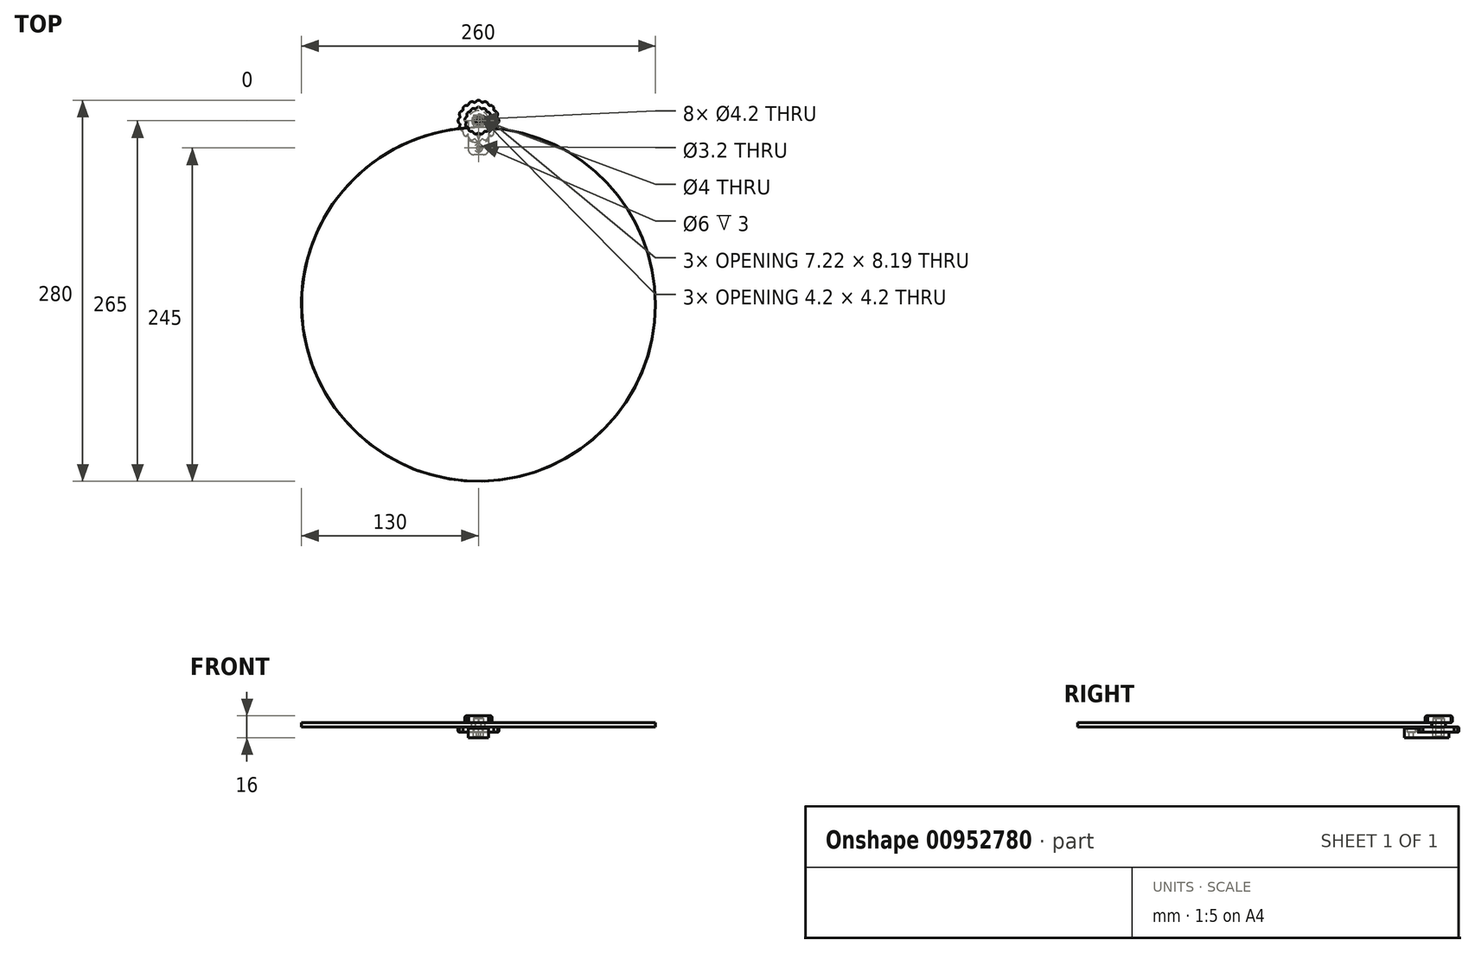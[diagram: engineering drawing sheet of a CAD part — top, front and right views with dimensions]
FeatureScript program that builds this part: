
annotation { "Feature Type Name" : "Feature", "Feature Type Description" : "" }
export const myFeature = defineFeature(function(context is Context, id is Id, definition is map)
    precondition{}
    {
        {
            var Q0;
            Q0=qCreatedBy(makeId("Top.planeOp"),FACE);
            var sketch = newSketch(context, id + "F0", { "sketchPlane" : qUnion([Q0])});
            skCircle(sketch, "E0", {"center": v(0, 0) * mm, "radius": 130 * mm});
            skSolve(sketch);
        }
        {
            var Q0;
            Q0=qCreatedBy(makeId("Top.planeOp"),FACE);
            var sketch = newSketch(context, id + "F1", { "sketchPlane" : qUnion([Q0])});
            skArc(sketch, "E1.0", {"start": v(7.5, 119.77) * mm, "mid": v(0, 120) * mm, "end": v(-7.5, 119.77) * mm});
            skLineSegment(sketch, "E2", {"start": v(0, 146.3) * mm, "end": v(0, 110.4) * mm});
            skLineSegment(sketch, "E3.0", {"start": v(-7.5, 146.3) * mm, "end": v(-7.5, 110.4) * mm});
            skLineSegment(sketch, "E4.0", {"start": v(7.5, 146.3) * mm, "end": v(7.5, 110.4) * mm});
            skArc(sketch, "E5.0", {"start": v(7.5, 129.78) * mm, "mid": v(0, 130) * mm, "end": v(-7.5, 129.78) * mm});
            skArc(sketch, "E6", {"start": v(7.5, 132.5) * mm, "mid": v(0, 140) * mm, "end": v(-7.5, 132.5) * mm});
            skSolve(sketch);
        }
        {
            var Q0;
            Q0 = qSketchRegion(id + "F1", true);
            extrude(context, id + "F2", {"entities" : qUnion([Q0]), "depth" : 4 * mm, "offsetDistance" : 25 * mm});
        }
        {
            var Q0;
            Q0=makeQuery(id+"F2.opExtrude","CAP_FACE",FACE,{"disambiguationData":[OSD([sQuery(id+"F1.wireOp",EDGE,"E1.0"),sQuery(id+"F1.wireOp",EDGE,"E3.0"),sQuery(id+"F1.wireOp",EDGE,"E4.0"),sQuery(id+"F1.wireOp",EDGE,"E6")])],"isStart":false});
            var sketch = newSketch(context, id + "F3", { "sketchPlane" : qUnion([Q0])});
            skArc(sketch, "E7.0", {"start": v(7.5, 129.78) * mm, "mid": v(0, 130) * mm, "end": v(-7.5, 129.78) * mm});
            skLineSegment(sketch, "E8.0", {"start": v(-7.5, 132.5) * mm, "end": v(-7.5, 119.77) * mm});
            skPoint(sketch, "E9.0", {"position": v(7.5, 132.5) * mm});
            skLineSegment(sketch, "E10.0", {"start": v(7.5, 132.5) * mm, "end": v(7.5, 119.77) * mm});
            skArc(sketch, "E11.0", {"start": v(7.5, 119.77) * mm, "mid": v(0, 120) * mm, "end": v(-7.5, 119.77) * mm});
            skSolve(sketch);
        }
        {
            var Q0;
            Q0 = qSketchRegion(id + "F3", true);
            extrude(context, id + "F4", {"entities" : qUnion([Q0]), "operationType" : NewBodyOperationType.REMOVE, "oppositeDirection" : true, "depth" : 3 * mm, "offsetDistance" : 25 * mm});
        }
        {
            var Q0;
            Q0=makeQuery(id+"F2.opExtrude","SWEPT_EDGE",EDGE,{"disambiguationData":[OSD([sQuery(id+"F1.wireOp",EDGE,"E1.0"),sQuery(id+"F1.wireOp",EDGE,"E4.0")])]});
            var Q1;
            Q1=makeQuery(id+"F2.opExtrude","SWEPT_EDGE",EDGE,{"disambiguationData":[OSD([sQuery(id+"F1.wireOp",EDGE,"E1.0"),sQuery(id+"F1.wireOp",EDGE,"E3.0")])]});
            fillet(context, id + "F5", {"entities" : qUnion([Q0, Q1]), "radius" : 5 * mm, "tangentPropagation" : true, "allowEdgeOverflow" : false});
        }
        {
            var Q0;
            Q0=makeQuery(id+"F2.opExtrude","CAP_FACE",FACE,{"disambiguationData":[OSD([sQuery(id+"F1.wireOp",EDGE,"E1.0"),sQuery(id+"F1.wireOp",EDGE,"E3.0"),sQuery(id+"F1.wireOp",EDGE,"E4.0"),sQuery(id+"F1.wireOp",EDGE,"E6")])],"isStart":false});
            var sketch = newSketch(context, id + "F6", { "sketchPlane" : qUnion([Q0])});
            skLineSegment(sketch, "E12", {"start": v(0, 140) * mm, "end": v(0, 130) * mm, "construction": true});
            skCircle(sketch, "E13", {"center": v(0, 135) * mm, "radius": 1.6 * mm});
            skSolve(sketch);
        }
        {
            var Q0;
            Q0=makeQuery(id+"F6.imprint","IMPRINT",FACE,{"disambiguationData":[TD([[makeQuery(id+"F6.imprint","IMPRINT",EDGE,{"derivedFrom":sQuery(id+"F6.wireOp",EDGE,"E13")}),1.0]])]});
            extrude(context, id + "F7", {"entities" : qUnion([Q0]), "operationType" : NewBodyOperationType.REMOVE, "oppositeDirection" : true, "depth" : 25 * mm, "offsetDistance" : 25 * mm});
        }
        {
            var Q0;
            Q0=makeQuery(id+"F2.opExtrude","CAP_FACE",FACE,{"disambiguationData":[OSD([sQuery(id+"F1.wireOp",EDGE,"E1.0"),sQuery(id+"F1.wireOp",EDGE,"E3.0"),sQuery(id+"F1.wireOp",EDGE,"E4.0"),sQuery(id+"F1.wireOp",EDGE,"E6")])],"isStart":true});
            var sketch = newSketch(context, id + "F8", { "sketchPlane" : qUnion([Q0])});
            skPoint(sketch, "E14.center", {"position": v(0, -135) * mm});
            skArc(sketch, "E15", {"start": v(-1.6, -144.19) * mm, "mid": v(0, -145) * mm, "end": v(1.6, -144.19) * mm});
            skArc(sketch, "E16.1.0", {"start": v(2.85, -143.88) * mm, "mid": v(4.65, -143.85) * mm, "end": v(5.7, -142.39) * mm});
            skArc(sketch, "E16.2.0", {"start": v(6.65, -141.54) * mm, "mid": v(8.23, -140.68) * mm, "end": v(8.48, -138.9) * mm});
            skArc(sketch, "E16.3.0", {"start": v(8.93, -137.7) * mm, "mid": v(9.93, -136.2) * mm, "end": v(9.32, -134.51) * mm});
            skArc(sketch, "E16.4.0", {"start": v(9.16, -133.24) * mm, "mid": v(9.35, -131.45) * mm, "end": v(8.02, -130.24) * mm});
            skArc(sketch, "E16.5.0", {"start": v(7.3, -129.19) * mm, "mid": v(6.63, -127.51) * mm, "end": v(4.9, -127.06) * mm});
            skArc(sketch, "E16.6.0", {"start": v(3.76, -126.46) * mm, "mid": v(2.4, -125.3) * mm, "end": v(0.64, -125.7) * mm});
            skArc(sketch, "E16.7.0", {"start": v(-0.64, -125.7) * mm, "mid": v(-2.4, -125.3) * mm, "end": v(-3.76, -126.46) * mm});
            skArc(sketch, "E16.8.0", {"start": v(-4.9, -127.06) * mm, "mid": v(-6.63, -127.51) * mm, "end": v(-7.3, -129.19) * mm});
            skArc(sketch, "E16.9.0", {"start": v(-8.02, -130.24) * mm, "mid": v(-9.35, -131.45) * mm, "end": v(-9.16, -133.24) * mm});
            skArc(sketch, "E16.10.0", {"start": v(-9.32, -134.51) * mm, "mid": v(-9.93, -136.2) * mm, "end": v(-8.93, -137.7) * mm});
            skArc(sketch, "E16.11.0", {"start": v(-8.48, -138.9) * mm, "mid": v(-8.23, -140.68) * mm, "end": v(-6.65, -141.54) * mm});
            skArc(sketch, "E16.12.0", {"start": v(-5.7, -142.39) * mm, "mid": v(-4.65, -143.85) * mm, "end": v(-2.85, -143.88) * mm});
            skPoint(sketch, "E17.newPointA", {"position": v(-5.25, -141.04) * mm});
            skPoint(sketch, "E17.newPointB", {"position": v(-5.36, -140.94) * mm});
            skArc(sketch, "E17.filletArc", {"start": v(-5.7, -142.39) * mm, "mid": v(-6.02, -141.8) * mm, "end": v(-6.65, -141.54) * mm});
            skPoint(sketch, "E18.newPointA", {"position": v(-1.84, -142.78) * mm});
            skPoint(sketch, "E18.newPointB", {"position": v(-1.98, -142.75) * mm});
            skArc(sketch, "E18.filletArc", {"start": v(-1.6, -144.19) * mm, "mid": v(-2.17, -143.81) * mm, "end": v(-2.85, -143.88) * mm});
            skPoint(sketch, "E19.newPointA", {"position": v(1.98, -142.75) * mm});
            skPoint(sketch, "E19.newPointB", {"position": v(1.84, -142.78) * mm});
            skArc(sketch, "E19.filletArc", {"start": v(2.85, -143.88) * mm, "mid": v(2.17, -143.81) * mm, "end": v(1.6, -144.19) * mm});
            skPoint(sketch, "E20.newPointA", {"position": v(5.36, -140.94) * mm});
            skPoint(sketch, "E20.newPointB", {"position": v(5.25, -141.04) * mm});
            skArc(sketch, "E20.filletArc", {"start": v(6.65, -141.54) * mm, "mid": v(6.02, -141.8) * mm, "end": v(5.7, -142.39) * mm});
            skPoint(sketch, "E21.newPointA", {"position": v(7.5, -137.77) * mm});
            skPoint(sketch, "E21.newPointB", {"position": v(7.45, -137.9) * mm});
            skArc(sketch, "E21.filletArc", {"start": v(8.93, -137.7) * mm, "mid": v(8.49, -138.22) * mm, "end": v(8.48, -138.9) * mm});
            skPoint(sketch, "E22.newPointA", {"position": v(7.93, -133.96) * mm});
            skPoint(sketch, "E22.newPointB", {"position": v(7.95, -134.1) * mm});
            skArc(sketch, "E22.filletArc", {"start": v(9.16, -133.24) * mm, "mid": v(9.01, -133.9) * mm, "end": v(9.32, -134.51) * mm});
            skPoint(sketch, "E23.newPointA", {"position": v(6.54, -130.4) * mm});
            skPoint(sketch, "E23.newPointB", {"position": v(6.62, -130.51) * mm});
            skArc(sketch, "E23.filletArc", {"start": v(7.3, -129.19) * mm, "mid": v(7.47, -129.84) * mm, "end": v(8.02, -130.24) * mm});
            skPoint(sketch, "E24.newPointA", {"position": v(3.65, -127.88) * mm});
            skPoint(sketch, "E24.newPointB", {"position": v(3.78, -127.95) * mm});
            skArc(sketch, "E24.filletArc", {"start": v(3.76, -126.46) * mm, "mid": v(4.22, -126.96) * mm, "end": v(4.9, -127.06) * mm});
            skPoint(sketch, "E25.newPointA", {"position": v(-0.07, -127) * mm});
            skPoint(sketch, "E25.newPointB", {"position": v(0.07, -127) * mm});
            skArc(sketch, "E25.filletArc", {"start": v(-0.64, -125.7) * mm, "mid": v(0, -125.92) * mm, "end": v(0.64, -125.7) * mm});
            skPoint(sketch, "E26.newPointA", {"position": v(-3.78, -127.95) * mm});
            skPoint(sketch, "E26.newPointB", {"position": v(-3.65, -127.88) * mm});
            skArc(sketch, "E26.filletArc", {"start": v(-4.9, -127.06) * mm, "mid": v(-4.22, -126.96) * mm, "end": v(-3.76, -126.46) * mm});
            skPoint(sketch, "E27.newPointA", {"position": v(-6.54, -130.4) * mm});
            skPoint(sketch, "E27.newPointB", {"position": v(-6.62, -130.51) * mm});
            skArc(sketch, "E27.filletArc", {"start": v(-8.02, -130.24) * mm, "mid": v(-7.47, -129.84) * mm, "end": v(-7.3, -129.19) * mm});
            skPoint(sketch, "E28.newPointA", {"position": v(-7.95, -134.1) * mm});
            skPoint(sketch, "E28.newPointB", {"position": v(-7.93, -133.96) * mm});
            skArc(sketch, "E28.filletArc", {"start": v(-9.32, -134.51) * mm, "mid": v(-9.01, -133.9) * mm, "end": v(-9.16, -133.24) * mm});
            skPoint(sketch, "E29.newPointA", {"position": v(-7.45, -137.9) * mm});
            skPoint(sketch, "E29.newPointB", {"position": v(-7.5, -137.77) * mm});
            skArc(sketch, "E29.filletArc", {"start": v(-8.48, -138.9) * mm, "mid": v(-8.49, -138.22) * mm, "end": v(-8.93, -137.7) * mm});
            skSolve(sketch);
        }
        {
            var Q0;
            Q0 = qSketchRegion(id + "F8", true);
            extrude(context, id + "F9", {"entities" : qUnion([Q0]), "depth" : 5 * mm, "offsetDistance" : 25 * mm});
        }
        {
            var Q0;
            Q0=makeQuery(id+"F9.opExtrude","CAP_FACE",FACE,{"disambiguationData":[OSD([sQuery(id+"F8.wireOp",EDGE,"E15"),sQuery(id+"F8.wireOp",EDGE,"E16.1.0"),sQuery(id+"F8.wireOp",EDGE,"E16.2.0"),sQuery(id+"F8.wireOp",EDGE,"E16.3.0"),sQuery(id+"F8.wireOp",EDGE,"E16.4.0"),sQuery(id+"F8.wireOp",EDGE,"E16.5.0"),sQuery(id+"F8.wireOp",EDGE,"E16.6.0"),sQuery(id+"F8.wireOp",EDGE,"E16.7.0"),sQuery(id+"F8.wireOp",EDGE,"E16.8.0"),sQuery(id+"F8.wireOp",EDGE,"E16.9.0"),sQuery(id+"F8.wireOp",EDGE,"E16.10.0"),sQuery(id+"F8.wireOp",EDGE,"E16.11.0"),sQuery(id+"F8.wireOp",EDGE,"E16.12.0"),sQuery(id+"F8.wireOp",EDGE,"E17.filletArc"),sQuery(id+"F8.wireOp",EDGE,"E18.filletArc"),sQuery(id+"F8.wireOp",EDGE,"E19.filletArc"),sQuery(id+"F8.wireOp",EDGE,"E20.filletArc"),sQuery(id+"F8.wireOp",EDGE,"E21.filletArc"),sQuery(id+"F8.wireOp",EDGE,"E22.filletArc"),sQuery(id+"F8.wireOp",EDGE,"E23.filletArc"),sQuery(id+"F8.wireOp",EDGE,"E24.filletArc"),sQuery(id+"F8.wireOp",EDGE,"E25.filletArc"),sQuery(id+"F8.wireOp",EDGE,"E26.filletArc"),sQuery(id+"F8.wireOp",EDGE,"E27.filletArc"),sQuery(id+"F8.wireOp",EDGE,"E28.filletArc"),sQuery(id+"F8.wireOp",EDGE,"E29.filletArc")])],"isStart":true});
            var Q1;
            Q1=makeQuery(id+"F9.opExtrude","CAP_FACE",FACE,{"disambiguationData":[OSD([sQuery(id+"F8.wireOp",EDGE,"E15"),sQuery(id+"F8.wireOp",EDGE,"E16.1.0"),sQuery(id+"F8.wireOp",EDGE,"E16.2.0"),sQuery(id+"F8.wireOp",EDGE,"E16.3.0"),sQuery(id+"F8.wireOp",EDGE,"E16.4.0"),sQuery(id+"F8.wireOp",EDGE,"E16.5.0"),sQuery(id+"F8.wireOp",EDGE,"E16.6.0"),sQuery(id+"F8.wireOp",EDGE,"E16.7.0"),sQuery(id+"F8.wireOp",EDGE,"E16.8.0"),sQuery(id+"F8.wireOp",EDGE,"E16.9.0"),sQuery(id+"F8.wireOp",EDGE,"E16.10.0"),sQuery(id+"F8.wireOp",EDGE,"E16.11.0"),sQuery(id+"F8.wireOp",EDGE,"E16.12.0"),sQuery(id+"F8.wireOp",EDGE,"E17.filletArc"),sQuery(id+"F8.wireOp",EDGE,"E18.filletArc"),sQuery(id+"F8.wireOp",EDGE,"E19.filletArc"),sQuery(id+"F8.wireOp",EDGE,"E20.filletArc"),sQuery(id+"F8.wireOp",EDGE,"E21.filletArc"),sQuery(id+"F8.wireOp",EDGE,"E22.filletArc"),sQuery(id+"F8.wireOp",EDGE,"E23.filletArc"),sQuery(id+"F8.wireOp",EDGE,"E24.filletArc"),sQuery(id+"F8.wireOp",EDGE,"E25.filletArc"),sQuery(id+"F8.wireOp",EDGE,"E26.filletArc"),sQuery(id+"F8.wireOp",EDGE,"E27.filletArc"),sQuery(id+"F8.wireOp",EDGE,"E28.filletArc"),sQuery(id+"F8.wireOp",EDGE,"E29.filletArc")])],"isStart":false});
            fillet(context, id + "F10", {"entities" : qUnion([Q0, Q1]), "radius" : 1 * mm, "tangentPropagation" : true, "allowEdgeOverflow" : false});
        }
        {
            var Q0;
            Q0=makeQuery(id+"F9.opExtrude","CAP_FACE",FACE,{"disambiguationData":[OSD([sQuery(id+"F8.wireOp",EDGE,"E15"),sQuery(id+"F8.wireOp",EDGE,"E16.1.0"),sQuery(id+"F8.wireOp",EDGE,"E16.2.0"),sQuery(id+"F8.wireOp",EDGE,"E16.3.0"),sQuery(id+"F8.wireOp",EDGE,"E16.4.0"),sQuery(id+"F8.wireOp",EDGE,"E16.5.0"),sQuery(id+"F8.wireOp",EDGE,"E16.6.0"),sQuery(id+"F8.wireOp",EDGE,"E16.7.0"),sQuery(id+"F8.wireOp",EDGE,"E16.8.0"),sQuery(id+"F8.wireOp",EDGE,"E16.9.0"),sQuery(id+"F8.wireOp",EDGE,"E16.10.0"),sQuery(id+"F8.wireOp",EDGE,"E16.11.0"),sQuery(id+"F8.wireOp",EDGE,"E16.12.0"),sQuery(id+"F8.wireOp",EDGE,"E17.filletArc"),sQuery(id+"F8.wireOp",EDGE,"E18.filletArc"),sQuery(id+"F8.wireOp",EDGE,"E19.filletArc"),sQuery(id+"F8.wireOp",EDGE,"E20.filletArc"),sQuery(id+"F8.wireOp",EDGE,"E21.filletArc"),sQuery(id+"F8.wireOp",EDGE,"E22.filletArc"),sQuery(id+"F8.wireOp",EDGE,"E23.filletArc"),sQuery(id+"F8.wireOp",EDGE,"E24.filletArc"),sQuery(id+"F8.wireOp",EDGE,"E25.filletArc"),sQuery(id+"F8.wireOp",EDGE,"E26.filletArc"),sQuery(id+"F8.wireOp",EDGE,"E27.filletArc"),sQuery(id+"F8.wireOp",EDGE,"E28.filletArc"),sQuery(id+"F8.wireOp",EDGE,"E29.filletArc")])],"isStart":false});
            var sketch = newSketch(context, id + "F11", { "sketchPlane" : qUnion([Q0])});
            skCircle(sketch, "E30", {"center": v(0, -135) * mm, "radius": 4.9 * mm});
            skSolve(sketch);
        }
        {
            var Q0;
            Q0 = qSketchRegion(id + "F11", true);
            extrude(context, id + "F12", {"entities" : qUnion([Q0]), "depth" : 3 * mm, "offsetDistance" : 25 * mm});
        }
        {
            var Q0;
            Q0=makeQuery(id+"F12.opExtrude","CAP_FACE",FACE,{"disambiguationData":[OSD([sQuery(id+"F11.wireOp",EDGE,"E30")])],"isStart":false});
            var sketch = newSketch(context, id + "F13", { "sketchPlane" : qUnion([Q0])});
            skLineSegment(sketch, "E31", {"start": v(0, -135) * mm, "end": v(17.48, -135) * mm, "construction": true});
            skArc(sketch, "E32", {"start": v(12.25, -137.49) * mm, "mid": v(15, -135) * mm, "end": v(12.25, -132.51) * mm});
            skArc(sketch, "E33.1.0", {"start": v(12.27, -132.61) * mm, "mid": v(13.86, -129.26) * mm, "end": v(10.37, -128.01) * mm});
            skArc(sketch, "E33.2.0", {"start": v(10.42, -128.1) * mm, "mid": v(10.6, -124.4) * mm, "end": v(6.9, -124.58) * mm});
            skArc(sketch, "E33.3.0", {"start": v(6.99, -124.63) * mm, "mid": v(5.74, -121.14) * mm, "end": v(2.39, -122.73) * mm});
            skArc(sketch, "E33.4.0", {"start": v(2.49, -122.75) * mm, "mid": v(0, -120) * mm, "end": v(-2.49, -122.75) * mm});
            skArc(sketch, "E33.5.0", {"start": v(-2.39, -122.73) * mm, "mid": v(-5.74, -121.14) * mm, "end": v(-6.99, -124.63) * mm});
            skArc(sketch, "E33.6.0", {"start": v(-6.9, -124.58) * mm, "mid": v(-10.6, -124.4) * mm, "end": v(-10.42, -128.1) * mm});
            skArc(sketch, "E33.7.0", {"start": v(-10.37, -128.01) * mm, "mid": v(-13.86, -129.26) * mm, "end": v(-12.27, -132.61) * mm});
            skArc(sketch, "E33.8.0", {"start": v(-12.25, -132.51) * mm, "mid": v(-15, -135) * mm, "end": v(-12.25, -137.49) * mm});
            skArc(sketch, "E33.9.0", {"start": v(-12.27, -137.39) * mm, "mid": v(-13.86, -140.74) * mm, "end": v(-10.37, -141.99) * mm});
            skArc(sketch, "E33.10.0", {"start": v(-10.42, -141.9) * mm, "mid": v(-10.6, -145.6) * mm, "end": v(-6.9, -145.42) * mm});
            skArc(sketch, "E33.11.0", {"start": v(-6.99, -145.37) * mm, "mid": v(-5.74, -148.86) * mm, "end": v(-2.39, -147.27) * mm});
            skArc(sketch, "E33.12.0", {"start": v(-2.49, -147.25) * mm, "mid": v(0, -150) * mm, "end": v(2.49, -147.25) * mm});
            skArc(sketch, "E33.13.0", {"start": v(2.39, -147.27) * mm, "mid": v(5.74, -148.86) * mm, "end": v(6.99, -145.37) * mm});
            skArc(sketch, "E33.14.0", {"start": v(6.9, -145.42) * mm, "mid": v(10.6, -145.6) * mm, "end": v(10.42, -141.9) * mm});
            skArc(sketch, "E33.15.0", {"start": v(10.37, -141.99) * mm, "mid": v(13.86, -140.74) * mm, "end": v(12.27, -137.39) * mm});
            skPoint(sketch, "E33.center", {"position": v(0, -135) * mm});
            skSolve(sketch);
        }
        {
            var Q0;
            Q0 = qSketchRegion(id + "F13", true);
            extrude(context, id + "F14", {"entities" : qUnion([Q0]), "operationType" : NewBodyOperationType.ADD, "depth" : 4 * mm, "offsetDistance" : 25 * mm});
        }
        {
            var Q0;
            Q0=makeQuery(id+"F14.opExtrude","SWEPT_EDGE",EDGE,{"disambiguationData":[OSD([sQuery(id+"F13.wireOp",EDGE,"E33.1.0"),sQuery(id+"F13.wireOp",EDGE,"E33.2.0")])]});
            var Q1;
            Q1=makeQuery(id+"F14.opExtrude","SWEPT_EDGE",EDGE,{"disambiguationData":[OSD([sQuery(id+"F13.wireOp",EDGE,"E32"),sQuery(id+"F13.wireOp",EDGE,"E33.1.0")])]});
            var Q2;
            Q2=makeQuery(id+"F14.opExtrude","SWEPT_EDGE",EDGE,{"disambiguationData":[OSD([sQuery(id+"F13.wireOp",EDGE,"E33.2.0"),sQuery(id+"F13.wireOp",EDGE,"E33.3.0")])]});
            var Q3;
            Q3=makeQuery(id+"F14.opExtrude","SWEPT_EDGE",EDGE,{"disambiguationData":[OSD([sQuery(id+"F13.wireOp",EDGE,"E33.3.0"),sQuery(id+"F13.wireOp",EDGE,"E33.4.0")])]});
            var Q4;
            Q4=makeQuery(id+"F14.opExtrude","SWEPT_EDGE",EDGE,{"disambiguationData":[OSD([sQuery(id+"F13.wireOp",EDGE,"E33.4.0"),sQuery(id+"F13.wireOp",EDGE,"E33.5.0")])]});
            var Q5;
            Q5=makeQuery(id+"F14.opExtrude","SWEPT_EDGE",EDGE,{"disambiguationData":[OSD([sQuery(id+"F13.wireOp",EDGE,"E33.5.0"),sQuery(id+"F13.wireOp",EDGE,"E33.6.0")])]});
            var Q6;
            Q6=makeQuery(id+"F14.opExtrude","SWEPT_EDGE",EDGE,{"disambiguationData":[OSD([sQuery(id+"F13.wireOp",EDGE,"E33.6.0"),sQuery(id+"F13.wireOp",EDGE,"E33.7.0")])]});
            var Q7;
            Q7=makeQuery(id+"F14.opExtrude","SWEPT_EDGE",EDGE,{"disambiguationData":[OSD([sQuery(id+"F13.wireOp",EDGE,"E33.7.0"),sQuery(id+"F13.wireOp",EDGE,"E33.8.0")])]});
            var Q8;
            Q8=makeQuery(id+"F14.opExtrude","SWEPT_EDGE",EDGE,{"disambiguationData":[OSD([sQuery(id+"F13.wireOp",EDGE,"E33.8.0"),sQuery(id+"F13.wireOp",EDGE,"E33.9.0")])]});
            var Q9;
            Q9=makeQuery(id+"F14.opExtrude","SWEPT_EDGE",EDGE,{"disambiguationData":[OSD([sQuery(id+"F13.wireOp",EDGE,"E33.9.0"),sQuery(id+"F13.wireOp",EDGE,"E33.10.0")])]});
            var Q10;
            Q10=makeQuery(id+"F14.opExtrude","SWEPT_EDGE",EDGE,{"disambiguationData":[OSD([sQuery(id+"F13.wireOp",EDGE,"E33.10.0"),sQuery(id+"F13.wireOp",EDGE,"E33.11.0")])]});
            var Q11;
            Q11=makeQuery(id+"F14.opExtrude","SWEPT_EDGE",EDGE,{"disambiguationData":[OSD([sQuery(id+"F13.wireOp",EDGE,"E33.11.0"),sQuery(id+"F13.wireOp",EDGE,"E33.12.0")])]});
            var Q12;
            Q12=makeQuery(id+"F14.opExtrude","SWEPT_EDGE",EDGE,{"disambiguationData":[OSD([sQuery(id+"F13.wireOp",EDGE,"E33.12.0"),sQuery(id+"F13.wireOp",EDGE,"E33.13.0")])]});
            var Q13;
            Q13=makeQuery(id+"F14.opExtrude","SWEPT_EDGE",EDGE,{"disambiguationData":[OSD([sQuery(id+"F13.wireOp",EDGE,"E33.13.0"),sQuery(id+"F13.wireOp",EDGE,"E33.14.0")])]});
            var Q14;
            Q14=makeQuery(id+"F14.opExtrude","SWEPT_EDGE",EDGE,{"disambiguationData":[OSD([sQuery(id+"F13.wireOp",EDGE,"E33.14.0"),sQuery(id+"F13.wireOp",EDGE,"E33.15.0")])]});
            var Q15;
            Q15=makeQuery(id+"F14.opExtrude","SWEPT_EDGE",EDGE,{"disambiguationData":[OSD([sQuery(id+"F13.wireOp",EDGE,"E32"),sQuery(id+"F13.wireOp",EDGE,"E33.15.0")])]});
            fillet(context, id + "F15", {"entities" : qUnion([Q0, Q1, Q2, Q3, Q4, Q5, Q6, Q7, Q8, Q9, Q10, Q11, Q12, Q13, Q14, Q15]), "radius" : 1 * mm, "tangentPropagation" : true, "allowEdgeOverflow" : false});
        }
        {
            var Q0;
            Q0=makeQuery(id+"F14.opExtrude","CAP_EDGE",EDGE,{"disambiguationData":[OSD([sQuery(id+"F13.wireOp",EDGE,"E33.13.0")])],"isStart":true});
            var Q1;
            Q1=makeQuery(id+"F14.opExtrude","CAP_EDGE",EDGE,{"disambiguationData":[OSD([sQuery(id+"F13.wireOp",EDGE,"E33.14.0")])],"isStart":false});
            fillet(context, id + "F16", {"entities" : qUnion([Q0, Q1]), "radius" : 1 * mm, "tangentPropagation" : true, "allowEdgeOverflow" : false});
        }
        {
            var Q0;
            Q0=makeQuery(id+"F2.opExtrude","SWEPT_BODY",BODY,{"disambiguationData":[OSD([sQuery(id+"F1.wireOp",EDGE,"E1.0"),sQuery(id+"F1.wireOp",EDGE,"E3.0"),sQuery(id+"F1.wireOp",EDGE,"E4.0"),sQuery(id+"F1.wireOp",EDGE,"E6")])]});
            deleteBodies(context, id + "F17", {"entities" : qUnion([Q0])});
        }
        {
            var Q0;
            Q0=makeQuery(id+"F9.opExtrude","CAP_FACE",FACE,{"disambiguationData":[OSD([sQuery(id+"F8.wireOp",EDGE,"E15"),sQuery(id+"F8.wireOp",EDGE,"E16.1.0"),sQuery(id+"F8.wireOp",EDGE,"E16.2.0"),sQuery(id+"F8.wireOp",EDGE,"E16.3.0"),sQuery(id+"F8.wireOp",EDGE,"E16.4.0"),sQuery(id+"F8.wireOp",EDGE,"E16.5.0"),sQuery(id+"F8.wireOp",EDGE,"E16.6.0"),sQuery(id+"F8.wireOp",EDGE,"E16.7.0"),sQuery(id+"F8.wireOp",EDGE,"E16.8.0"),sQuery(id+"F8.wireOp",EDGE,"E16.9.0"),sQuery(id+"F8.wireOp",EDGE,"E16.10.0"),sQuery(id+"F8.wireOp",EDGE,"E16.11.0"),sQuery(id+"F8.wireOp",EDGE,"E16.12.0"),sQuery(id+"F8.wireOp",EDGE,"E17.filletArc"),sQuery(id+"F8.wireOp",EDGE,"E18.filletArc"),sQuery(id+"F8.wireOp",EDGE,"E19.filletArc"),sQuery(id+"F8.wireOp",EDGE,"E20.filletArc"),sQuery(id+"F8.wireOp",EDGE,"E21.filletArc"),sQuery(id+"F8.wireOp",EDGE,"E22.filletArc"),sQuery(id+"F8.wireOp",EDGE,"E23.filletArc"),sQuery(id+"F8.wireOp",EDGE,"E24.filletArc"),sQuery(id+"F8.wireOp",EDGE,"E25.filletArc"),sQuery(id+"F8.wireOp",EDGE,"E26.filletArc"),sQuery(id+"F8.wireOp",EDGE,"E27.filletArc"),sQuery(id+"F8.wireOp",EDGE,"E28.filletArc"),sQuery(id+"F8.wireOp",EDGE,"E29.filletArc")])],"isStart":true});
            var sketch = newSketch(context, id + "F18", { "sketchPlane" : qUnion([Q0])});
            skLineSegment(sketch, "E34", {"start": v(-8.02, 134.03) * mm, "end": v(8.93, 136.08) * mm, "construction": true});
            skCircle(sketch, "E35", {"center": v(0, 135) * mm, "radius": 2.1 * mm});
            skSolve(sketch);
        }
        {
            var Q0;
            Q0 = qSketchRegion(id + "F18", true);
            extrude(context, id + "F19", {"entities" : qUnion([Q0]), "operationType" : NewBodyOperationType.REMOVE, "oppositeDirection" : true, "depth" : 25 * mm, "offsetDistance" : 25 * mm});
        }
        {
            var Q0;
            Q0=makeQuery(id+"F14.opExtrude","CAP_FACE",FACE,{"disambiguationData":[OSD([sQuery(id+"F13.wireOp",EDGE,"E32"),sQuery(id+"F13.wireOp",EDGE,"E33.1.0"),sQuery(id+"F13.wireOp",EDGE,"E33.2.0"),sQuery(id+"F13.wireOp",EDGE,"E33.3.0"),sQuery(id+"F13.wireOp",EDGE,"E33.4.0"),sQuery(id+"F13.wireOp",EDGE,"E33.5.0"),sQuery(id+"F13.wireOp",EDGE,"E33.6.0"),sQuery(id+"F13.wireOp",EDGE,"E33.7.0"),sQuery(id+"F13.wireOp",EDGE,"E33.8.0"),sQuery(id+"F13.wireOp",EDGE,"E33.9.0"),sQuery(id+"F13.wireOp",EDGE,"E33.10.0"),sQuery(id+"F13.wireOp",EDGE,"E33.11.0"),sQuery(id+"F13.wireOp",EDGE,"E33.12.0"),sQuery(id+"F13.wireOp",EDGE,"E33.13.0"),sQuery(id+"F13.wireOp",EDGE,"E33.14.0"),sQuery(id+"F13.wireOp",EDGE,"E33.15.0")])],"isStart":false});
            var sketch = newSketch(context, id + "F20", { "sketchPlane" : qUnion([Q0])});
            skCircle(sketch, "E36.cCircle", {"center": v(0, -135) * mm, "radius": 3.55 * mm, "construction": true});
            skLineSegment(sketch, "E36.0", {"start": v(3.55, -132.95) * mm, "end": v(3.55, -137.05) * mm});
            skLineSegment(sketch, "E36.1", {"start": v(3.55, -137.05) * mm, "end": v(0, -139.1) * mm});
            skLineSegment(sketch, "E36.2", {"start": v(0, -139.1) * mm, "end": v(-3.55, -137.05) * mm});
            skLineSegment(sketch, "E36.3", {"start": v(-3.55, -137.05) * mm, "end": v(-3.55, -132.95) * mm});
            skLineSegment(sketch, "E36.4", {"start": v(-3.55, -132.95) * mm, "end": v(0, -130.9) * mm});
            skLineSegment(sketch, "E36.5", {"start": v(0, -130.9) * mm, "end": v(3.55, -132.95) * mm});
            skPoint(sketch, "E36.0.midPoint", {"position": v(3.55, -135) * mm});
            skSolve(sketch);
        }
        {
            var Q0;
            Q0 = qSketchRegion(id + "F20", true);
            extrude(context, id + "F21", {"entities" : qUnion([Q0]), "operationType" : NewBodyOperationType.REMOVE, "oppositeDirection" : true, "depth" : 3.2 * mm, "offsetDistance" : 25 * mm});
        }
        {
            var Q0;
            Q0=makeQuery(id+"F9.opExtrude","CAP_FACE",FACE,{"disambiguationData":[OSD([sQuery(id+"F8.wireOp",EDGE,"E15"),sQuery(id+"F8.wireOp",EDGE,"E16.1.0"),sQuery(id+"F8.wireOp",EDGE,"E16.2.0"),sQuery(id+"F8.wireOp",EDGE,"E16.3.0"),sQuery(id+"F8.wireOp",EDGE,"E16.4.0"),sQuery(id+"F8.wireOp",EDGE,"E16.5.0"),sQuery(id+"F8.wireOp",EDGE,"E16.6.0"),sQuery(id+"F8.wireOp",EDGE,"E16.7.0"),sQuery(id+"F8.wireOp",EDGE,"E16.8.0"),sQuery(id+"F8.wireOp",EDGE,"E16.9.0"),sQuery(id+"F8.wireOp",EDGE,"E16.10.0"),sQuery(id+"F8.wireOp",EDGE,"E16.11.0"),sQuery(id+"F8.wireOp",EDGE,"E16.12.0"),sQuery(id+"F8.wireOp",EDGE,"E17.filletArc"),sQuery(id+"F8.wireOp",EDGE,"E18.filletArc"),sQuery(id+"F8.wireOp",EDGE,"E19.filletArc"),sQuery(id+"F8.wireOp",EDGE,"E20.filletArc"),sQuery(id+"F8.wireOp",EDGE,"E21.filletArc"),sQuery(id+"F8.wireOp",EDGE,"E22.filletArc"),sQuery(id+"F8.wireOp",EDGE,"E23.filletArc"),sQuery(id+"F8.wireOp",EDGE,"E24.filletArc"),sQuery(id+"F8.wireOp",EDGE,"E25.filletArc"),sQuery(id+"F8.wireOp",EDGE,"E26.filletArc"),sQuery(id+"F8.wireOp",EDGE,"E27.filletArc"),sQuery(id+"F8.wireOp",EDGE,"E28.filletArc"),sQuery(id+"F8.wireOp",EDGE,"E29.filletArc")])],"isStart":false});
            var sketch = newSketch(context, id + "F22", { "sketchPlane" : qUnion([Q0])});
            skCircle(sketch, "E37.cCircle", {"center": v(0, -135) * mm, "radius": 3.55 * mm, "construction": true});
            skLineSegment(sketch, "E37.0", {"start": v(3.49, -137.15) * mm, "end": v(-0.12, -139.1) * mm});
            skLineSegment(sketch, "E37.1", {"start": v(-0.12, -139.1) * mm, "end": v(-3.6, -136.94) * mm});
            skLineSegment(sketch, "E37.2", {"start": v(-3.6, -136.94) * mm, "end": v(-3.49, -132.85) * mm});
            skLineSegment(sketch, "E37.3", {"start": v(-3.49, -132.85) * mm, "end": v(0.12, -130.9) * mm});
            skLineSegment(sketch, "E37.4", {"start": v(0.12, -130.9) * mm, "end": v(3.6, -133.06) * mm});
            skLineSegment(sketch, "E37.5", {"start": v(3.6, -133.06) * mm, "end": v(3.49, -137.15) * mm});
            skPoint(sketch, "E37.0.midPoint", {"position": v(1.68, -138.13) * mm});
            skSolve(sketch);
        }
        {
            var Q0;
            Q0 = qSketchRegion(id + "F22", true);
            extrude(context, id + "F23", {"entities" : qUnion([Q0]), "operationType" : NewBodyOperationType.REMOVE, "oppositeDirection" : true, "depth" : 3.2 * mm, "offsetDistance" : 25 * mm});
        }
        {
            var Q0;
            Q0=makeQuery(id+"F14.opExtrude","CAP_FACE",FACE,{"disambiguationData":[OSD([sQuery(id+"F13.wireOp",EDGE,"E32"),sQuery(id+"F13.wireOp",EDGE,"E33.1.0"),sQuery(id+"F13.wireOp",EDGE,"E33.2.0"),sQuery(id+"F13.wireOp",EDGE,"E33.3.0"),sQuery(id+"F13.wireOp",EDGE,"E33.4.0"),sQuery(id+"F13.wireOp",EDGE,"E33.5.0"),sQuery(id+"F13.wireOp",EDGE,"E33.6.0"),sQuery(id+"F13.wireOp",EDGE,"E33.7.0"),sQuery(id+"F13.wireOp",EDGE,"E33.8.0"),sQuery(id+"F13.wireOp",EDGE,"E33.9.0"),sQuery(id+"F13.wireOp",EDGE,"E33.10.0"),sQuery(id+"F13.wireOp",EDGE,"E33.11.0"),sQuery(id+"F13.wireOp",EDGE,"E33.12.0"),sQuery(id+"F13.wireOp",EDGE,"E33.13.0"),sQuery(id+"F13.wireOp",EDGE,"E33.14.0"),sQuery(id+"F13.wireOp",EDGE,"E33.15.0")])],"isStart":false});
            var sketch = newSketch(context, id + "F24", { "sketchPlane" : qUnion([Q0])});
            skPoint(sketch, "E38.endSnap0", {"position": v(0, -121) * mm});
            skLineSegment(sketch, "E39.0", {"start": v(7.5, -135) * mm, "end": v(7.5, -114) * mm});
            skLineSegment(sketch, "E40.0", {"start": v(-7.5, -135) * mm, "end": v(-7.5, -114) * mm});
            skLineSegment(sketch, "E41.left", {"start": v(7.5, -135) * mm, "end": v(7.5, -135) * mm});
            skLineSegment(sketch, "E41.right", {"start": v(-7.5, -135) * mm, "end": v(-7.5, -135) * mm});
            skArc(sketch, "E42", {"start": v(-7.5, -135) * mm, "mid": v(0, -142.5) * mm, "end": v(7.5, -135) * mm});
            skLineSegment(sketch, "E43", {"start": v(3.5, -110) * mm, "end": v(-3.5, -110) * mm});
            skCircle(sketch, "E44", {"center": v(0, -115) * mm, "radius": 1.6 * mm});
            skArc(sketch, "E45.filletArc", {"start": v(7.5, -114) * mm, "mid": v(6.33, -111.17) * mm, "end": v(3.5, -110) * mm});
            skArc(sketch, "E46.filletArc", {"start": v(-3.5, -110) * mm, "mid": v(-6.33, -111.17) * mm, "end": v(-7.5, -114) * mm});
            skSolve(sketch);
        }
        {
            var Q0;
            Q0 = qSketchRegion(id + "F24", true);
            extrude(context, id + "F25", {"entities" : qUnion([Q0]), "depth" : 4 * mm, "offsetDistance" : 25 * mm});
        }
        {
            var Q0;
            Q0=makeQuery(id+"F25.opExtrude","CAP_FACE",FACE,{"disambiguationData":[OSD([sQuery(id+"F24.wireOp",EDGE,"E39.0"),sQuery(id+"F24.wireOp",EDGE,"E40.0"),sQuery(id+"F24.wireOp",EDGE,"E42"),sQuery(id+"F24.wireOp",EDGE,"E43"),sQuery(id+"F24.wireOp",EDGE,"E44"),sQuery(id+"F24.wireOp",EDGE,"E45.filletArc"),sQuery(id+"F24.wireOp",EDGE,"E46.filletArc")])],"isStart":true});
            var sketch = newSketch(context, id + "F26", { "sketchPlane" : qUnion([Q0])});
            skArc(sketch, "E47", {"start": v(-7.5, 120.87) * mm, "mid": v(0, 119) * mm, "end": v(7.5, 120.87) * mm});
            skLineSegment(sketch, "E48.0", {"start": v(7.5, 135) * mm, "end": v(7.5, 114) * mm});
            skPoint(sketch, "E49.0", {"position": v(6.33, 111.17) * mm});
            skArc(sketch, "E50.0", {"start": v(7.5, 114) * mm, "mid": v(6.33, 111.17) * mm, "end": v(3.5, 110) * mm});
            skLineSegment(sketch, "E51.0", {"start": v(3.5, 110) * mm, "end": v(-3.5, 110) * mm});
            skArc(sketch, "E52.0", {"start": v(-3.5, 110) * mm, "mid": v(-6.33, 111.17) * mm, "end": v(-7.5, 114) * mm});
            skLineSegment(sketch, "E53.0", {"start": v(-7.5, 135) * mm, "end": v(-7.5, 114) * mm});
            skSolve(sketch);
        }
        {
            var Q0;
            Q0 = qSketchRegion(id + "F26", true);
            extrude(context, id + "F27", {"entities" : qUnion([Q0]), "operationType" : NewBodyOperationType.ADD, "depth" : 3 * mm, "offsetDistance" : 25 * mm});
        }
        {
            var Q0;
            Q0=makeQuery(id+"F27.opExtrude","CAP_FACE",FACE,{"disambiguationData":[OSD([sQuery(id+"F26.wireOp",EDGE,"E47"),sQuery(id+"F26.wireOp",EDGE,"E48.0"),sQuery(id+"F26.wireOp",EDGE,"E50.0"),sQuery(id+"F26.wireOp",EDGE,"E51.0"),sQuery(id+"F26.wireOp",EDGE,"E52.0"),sQuery(id+"F26.wireOp",EDGE,"E53.0")])],"isStart":false});
            var sketch = newSketch(context, id + "F28", { "sketchPlane" : qUnion([Q0])});
            skCircle(sketch, "E54.0", {"center": v(0, 115) * mm, "radius": 1.6 * mm});
            skSolve(sketch);
        }
        {
            var Q0;
            Q0 = qSketchRegion(id + "F28", true);
            extrude(context, id + "F29", {"entities" : qUnion([Q0]), "operationType" : NewBodyOperationType.REMOVE, "oppositeDirection" : true, "depth" : 25 * mm, "offsetDistance" : 25 * mm});
        }
        {
            var Q0;
            Q0=makeQuery(id+"F25.opExtrude","CAP_FACE",FACE,{"disambiguationData":[OSD([sQuery(id+"F24.wireOp",EDGE,"E39.0"),sQuery(id+"F24.wireOp",EDGE,"E40.0"),sQuery(id+"F24.wireOp",EDGE,"E42"),sQuery(id+"F24.wireOp",EDGE,"E43"),sQuery(id+"F24.wireOp",EDGE,"E44"),sQuery(id+"F24.wireOp",EDGE,"E45.filletArc"),sQuery(id+"F24.wireOp",EDGE,"E46.filletArc")])],"isStart":false});
            var sketch = newSketch(context, id + "F30", { "sketchPlane" : qUnion([Q0])});
            skCircle(sketch, "E55", {"center": v(0, -135) * mm, "radius": 2 * mm});
            skSolve(sketch);
        }
        {
            var Q0;
            Q0 = qSketchRegion(id + "F30", true);
            extrude(context, id + "F31", {"entities" : qUnion([Q0]), "operationType" : NewBodyOperationType.REMOVE, "oppositeDirection" : true, "depth" : 25 * mm, "offsetDistance" : 25 * mm});
        }
        {
            var Q0;
            Q0=makeQuery(id+"F25.opExtrude","CAP_FACE",FACE,{"disambiguationData":[OSD([sQuery(id+"F24.wireOp",EDGE,"E39.0"),sQuery(id+"F24.wireOp",EDGE,"E40.0"),sQuery(id+"F24.wireOp",EDGE,"E42"),sQuery(id+"F24.wireOp",EDGE,"E43"),sQuery(id+"F24.wireOp",EDGE,"E44"),sQuery(id+"F24.wireOp",EDGE,"E45.filletArc"),sQuery(id+"F24.wireOp",EDGE,"E46.filletArc")])],"isStart":true});
            var sketch = newSketch(context, id + "F32", { "sketchPlane" : qUnion([Q0])});
            skCircle(sketch, "E56.cCircle", {"center": v(0, 135) * mm, "radius": 3.55 * mm, "construction": true});
            skLineSegment(sketch, "E56.0", {"start": v(3.55, 137.05) * mm, "end": v(3.55, 132.95) * mm});
            skLineSegment(sketch, "E56.1", {"start": v(3.55, 132.95) * mm, "end": v(0, 130.9) * mm});
            skLineSegment(sketch, "E56.2", {"start": v(0, 130.9) * mm, "end": v(-3.55, 132.95) * mm});
            skLineSegment(sketch, "E56.3", {"start": v(-3.55, 132.95) * mm, "end": v(-3.55, 137.05) * mm});
            skLineSegment(sketch, "E56.4", {"start": v(-3.55, 137.05) * mm, "end": v(0, 139.1) * mm});
            skLineSegment(sketch, "E56.5", {"start": v(0, 139.1) * mm, "end": v(3.55, 137.05) * mm});
            skPoint(sketch, "E56.0.midPoint", {"position": v(3.55, 135) * mm});
            skSolve(sketch);
        }
        {
            var Q0;
            Q0 = qSketchRegion(id + "F32", true);
            extrude(context, id + "F33", {"entities" : qUnion([Q0]), "operationType" : NewBodyOperationType.REMOVE, "oppositeDirection" : true, "depth" : 3.1 * mm, "offsetDistance" : 25 * mm});
        }
        {
            var Q0;
            Q0=makeQuery(id+"F27.opExtrude","CAP_FACE",FACE,{"disambiguationData":[OSD([sQuery(id+"F26.wireOp",EDGE,"E47"),sQuery(id+"F26.wireOp",EDGE,"E48.0"),sQuery(id+"F26.wireOp",EDGE,"E50.0"),sQuery(id+"F26.wireOp",EDGE,"E51.0"),sQuery(id+"F26.wireOp",EDGE,"E52.0"),sQuery(id+"F26.wireOp",EDGE,"E53.0")])],"isStart":false});
            var sketch = newSketch(context, id + "F34", { "sketchPlane" : qUnion([Q0])});
            skCircle(sketch, "E57", {"center": v(0, 115) * mm, "radius": 3 * mm});
            skSolve(sketch);
        }
        {
            var Q0;
            Q0 = qSketchRegion(id + "F34", true);
            extrude(context, id + "F35", {"entities" : qUnion([Q0]), "operationType" : NewBodyOperationType.REMOVE, "oppositeDirection" : true, "depth" : 3 * mm, "offsetDistance" : 25 * mm});
        }
        {
            var Q0;
            Q0=makeQuery(id+"F14.opExtrude","CAP_FACE",FACE,{"disambiguationData":[OSD([sQuery(id+"F13.wireOp",EDGE,"E32"),sQuery(id+"F13.wireOp",EDGE,"E33.1.0"),sQuery(id+"F13.wireOp",EDGE,"E33.2.0"),sQuery(id+"F13.wireOp",EDGE,"E33.3.0"),sQuery(id+"F13.wireOp",EDGE,"E33.4.0"),sQuery(id+"F13.wireOp",EDGE,"E33.5.0"),sQuery(id+"F13.wireOp",EDGE,"E33.6.0"),sQuery(id+"F13.wireOp",EDGE,"E33.7.0"),sQuery(id+"F13.wireOp",EDGE,"E33.8.0"),sQuery(id+"F13.wireOp",EDGE,"E33.9.0"),sQuery(id+"F13.wireOp",EDGE,"E33.10.0"),sQuery(id+"F13.wireOp",EDGE,"E33.11.0"),sQuery(id+"F13.wireOp",EDGE,"E33.12.0"),sQuery(id+"F13.wireOp",EDGE,"E33.13.0"),sQuery(id+"F13.wireOp",EDGE,"E33.14.0"),sQuery(id+"F13.wireOp",EDGE,"E33.15.0")])],"isStart":true});
            var sketch = newSketch(context, id + "F36", { "sketchPlane" : qUnion([Q0])});
            skCircle(sketch, "E58.0", {"center": v(0, 0) * mm, "radius": 130 * mm});
            skSolve(sketch);
        }
        {
            var Q0;
            Q0 = qSketchRegion(id + "F36", true);
            extrude(context, id + "F37", {"entities" : qUnion([Q0]), "depth" : 3 * mm, "offsetDistance" : 25 * mm});
        }
        {
            var Q0;
            Q0=makeQuery(id+"F14.opExtrude","CAP_FACE",FACE,{"disambiguationData":[OSD([sQuery(id+"F13.wireOp",EDGE,"E32"),sQuery(id+"F13.wireOp",EDGE,"E33.1.0"),sQuery(id+"F13.wireOp",EDGE,"E33.2.0"),sQuery(id+"F13.wireOp",EDGE,"E33.3.0"),sQuery(id+"F13.wireOp",EDGE,"E33.4.0"),sQuery(id+"F13.wireOp",EDGE,"E33.5.0"),sQuery(id+"F13.wireOp",EDGE,"E33.6.0"),sQuery(id+"F13.wireOp",EDGE,"E33.7.0"),sQuery(id+"F13.wireOp",EDGE,"E33.8.0"),sQuery(id+"F13.wireOp",EDGE,"E33.9.0"),sQuery(id+"F13.wireOp",EDGE,"E33.10.0"),sQuery(id+"F13.wireOp",EDGE,"E33.11.0"),sQuery(id+"F13.wireOp",EDGE,"E33.12.0"),sQuery(id+"F13.wireOp",EDGE,"E33.13.0"),sQuery(id+"F13.wireOp",EDGE,"E33.14.0"),sQuery(id+"F13.wireOp",EDGE,"E33.15.0")])],"isStart":true});
            var sketch = newSketch(context, id + "F38", { "sketchPlane" : qUnion([Q0])});
            skLineSegment(sketch, "E59", {"start": v(-1.25, 124.2) * mm, "end": v(1.25, 124.2) * mm});
            skLineSegment(sketch, "E60", {"start": v(-1.25, 124.2) * mm, "end": v(0, 121) * mm});
            skLineSegment(sketch, "E61", {"start": v(0, 121) * mm, "end": v(1.25, 124.2) * mm});
            skSolve(sketch);
        }
        {
            var Q0;
            Q0 = qSketchRegion(id + "F38", true);
            extrude(context, id + "F39", {"entities" : qUnion([Q0]), "operationType" : NewBodyOperationType.REMOVE, "oppositeDirection" : true, "depth" : .2 * mm, "offsetDistance" : 25 * mm});
        }
        {
            var Q0;
            Q0=makeQuery(id+"F27.opExtrude","SWEPT_EDGE",EDGE,{"disambiguationData":[OSD([sQuery(id+"F26.wireOp",EDGE,"E47"),sQuery(id+"F26.wireOp",EDGE,"E48.0")])]});
            var Q1;
            Q1=makeQuery(id+"F27.opExtrude","SWEPT_EDGE",EDGE,{"disambiguationData":[OSD([sQuery(id+"F26.wireOp",EDGE,"E47"),sQuery(id+"F26.wireOp",EDGE,"E53.0")])]});
            fillet(context, id + "F40", {"entities" : qUnion([Q0, Q1]), "radius" : 1 * mm, "tangentPropagation" : true, "allowEdgeOverflow" : false});
        }
        {
            var Q0;
            Q0=makeQuery(id+"F14.opExtrude","CAP_FACE",FACE,{"disambiguationData":[OSD([sQuery(id+"F13.wireOp",EDGE,"E32"),sQuery(id+"F13.wireOp",EDGE,"E33.1.0"),sQuery(id+"F13.wireOp",EDGE,"E33.2.0"),sQuery(id+"F13.wireOp",EDGE,"E33.3.0"),sQuery(id+"F13.wireOp",EDGE,"E33.4.0"),sQuery(id+"F13.wireOp",EDGE,"E33.5.0"),sQuery(id+"F13.wireOp",EDGE,"E33.6.0"),sQuery(id+"F13.wireOp",EDGE,"E33.7.0"),sQuery(id+"F13.wireOp",EDGE,"E33.8.0"),sQuery(id+"F13.wireOp",EDGE,"E33.9.0"),sQuery(id+"F13.wireOp",EDGE,"E33.10.0"),sQuery(id+"F13.wireOp",EDGE,"E33.11.0"),sQuery(id+"F13.wireOp",EDGE,"E33.12.0"),sQuery(id+"F13.wireOp",EDGE,"E33.13.0"),sQuery(id+"F13.wireOp",EDGE,"E33.14.0"),sQuery(id+"F13.wireOp",EDGE,"E33.15.0")])],"isStart":false});
            var sketch = newSketch(context, id + "F41", { "sketchPlane" : qUnion([Q0])});
            skCircle(sketch, "E62.0", {"center": v(0, -135) * mm, "radius": 2.1 * mm});
            skSolve(sketch);
        }
        {
            var Q0;
            Q0 = qSketchRegion(id + "F41", true);
            extrude(context, id + "F42", {"entities" : qUnion([Q0]), "operationType" : NewBodyOperationType.REMOVE, "oppositeDirection" : true, "depth" : 25 * mm, "offsetDistance" : 25 * mm});
        }
    });
